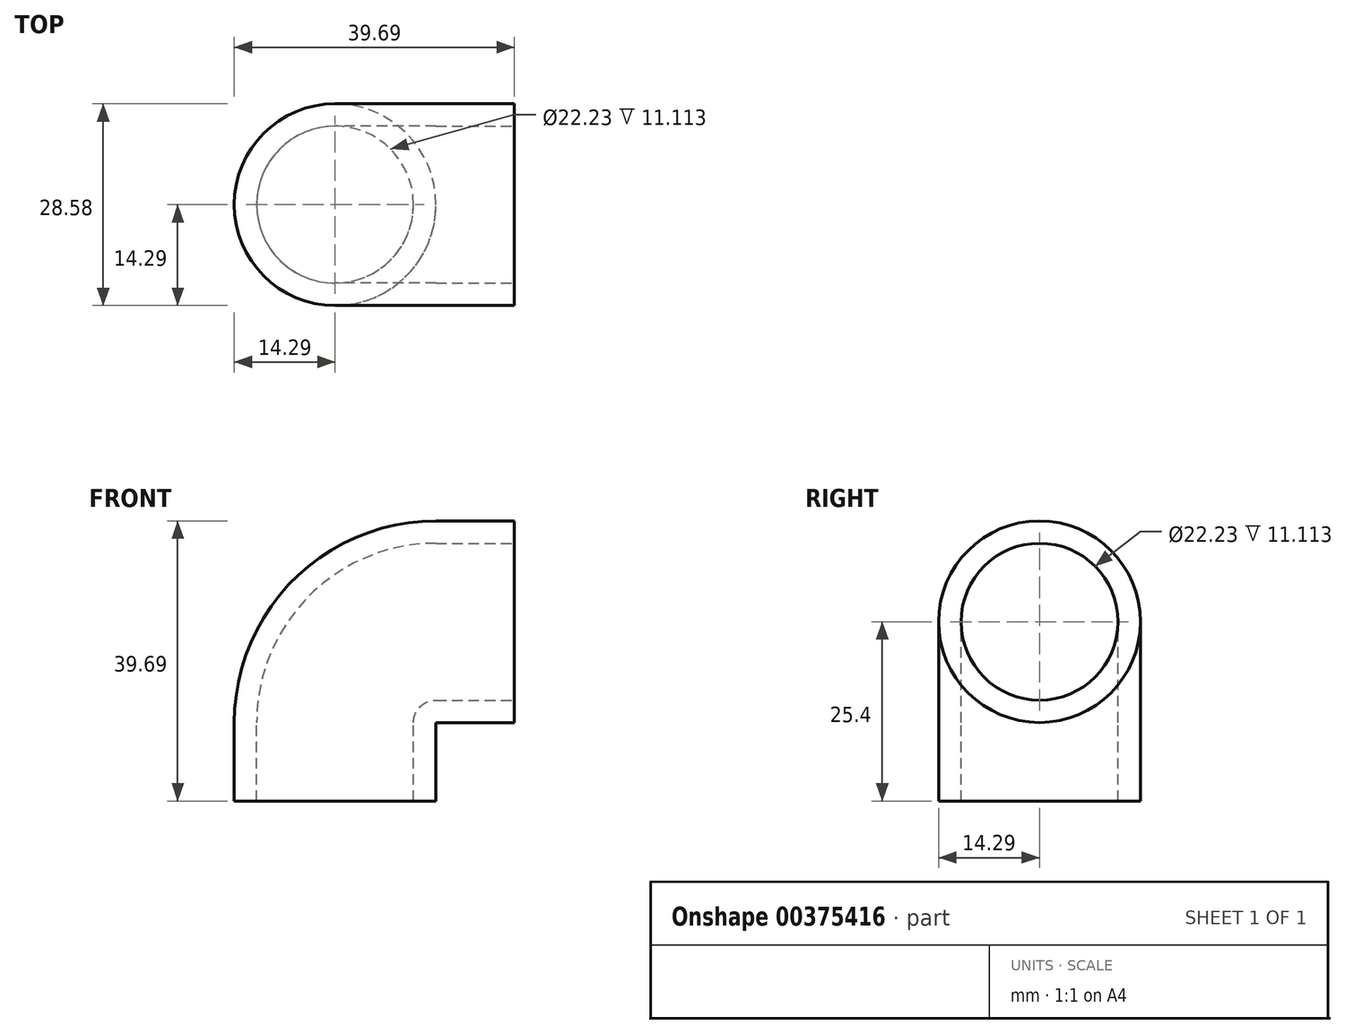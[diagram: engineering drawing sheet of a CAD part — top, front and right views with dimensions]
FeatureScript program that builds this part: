
annotation { "Feature Type Name" : "Feature", "Feature Type Description" : "" }
export const myFeature = defineFeature(function(context is Context, id is Id, definition is map)
    precondition{}
    {
        {
            var Q0;
            Q0=qCreatedBy(makeId("Top.planeOp"),FACE);
            var sketch = newSketch(context, id + "F0", { "sketchPlane" : qUnion([Q0])});
            skCircle(sketch, "E0", {"center": v(0, 0) * mm, "radius": 14.29 * mm});
            skCircle(sketch, "E1", {"center": v(0, 0) * mm, "radius": 11.11 * mm});
            skSolve(sketch);
        }
        {
            var Q0;
            Q0=qCreatedBy(makeId("Front.planeOp"),FACE);
            var sketch = newSketch(context, id + "F1", { "sketchPlane" : qUnion([Q0])});
            skLineSegment(sketch, "E2", {"start": v(0, 0) * mm, "end": v(0, 11.11) * mm});
            skArc(sketch, "E3", {"start": v(14.29, 25.4) * mm, "mid": v(4.18, 21.22) * mm, "end": v(0, 11.11) * mm});
            skLineSegment(sketch, "E4", {"start": v(14.29, 25.4) * mm, "end": v(25.4, 25.4) * mm});
            skSolve(sketch);
        }
        {
            var Q0;
            Q0=qSketchRegion(id+"F0",true);
            var Q1;
            Q1=qConstructionFilter(qBodyType(qCreatedBy(id+"F1",EDGE),BodyType.WIRE),ConstructionObject.NO);
            sweep(context, id + "F2", {"profiles" : qUnion([Q0]), "path" : qUnion([Q1])});
        }
    });
